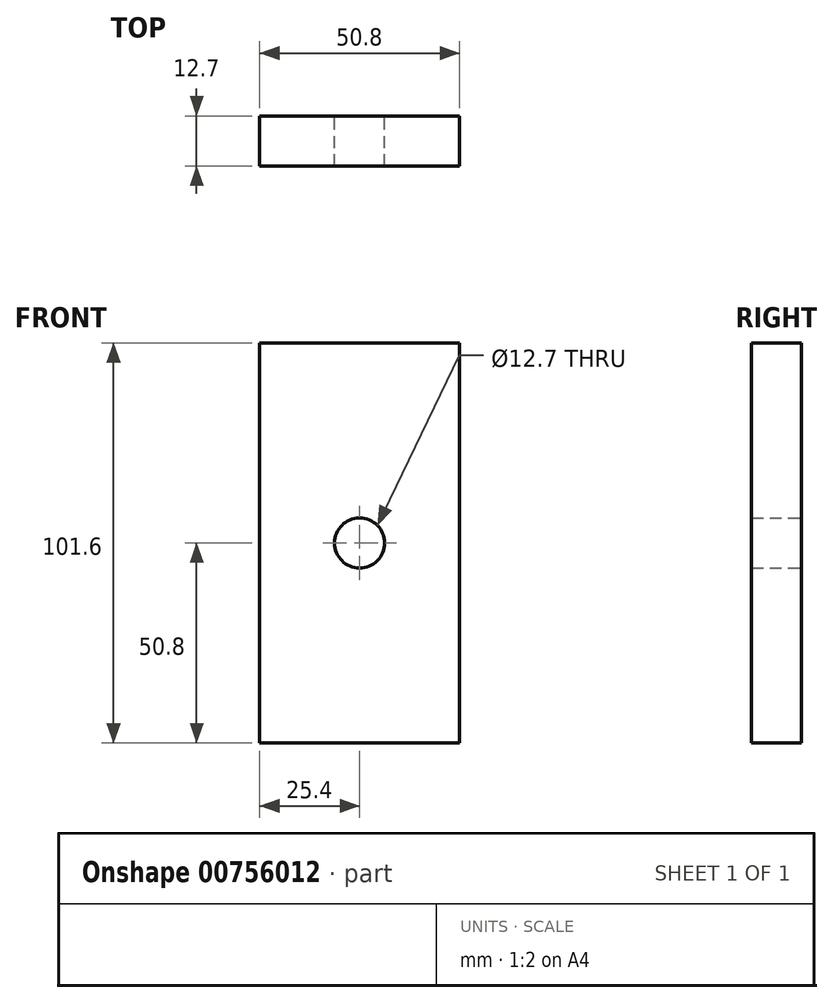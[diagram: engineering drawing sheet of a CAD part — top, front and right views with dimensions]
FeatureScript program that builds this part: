
annotation { "Feature Type Name" : "Feature", "Feature Type Description" : "" }
export const myFeature = defineFeature(function(context is Context, id is Id, definition is map)
    precondition{}
    {
        {
            var Q0;
            Q0=qCreatedBy(makeId("Front.planeOp"),FACE);
            var sketch = newSketch(context, id + "F0", { "sketchPlane" : qUnion([Q0])});
            skLineSegment(sketch, "E0.bottom", {"start": v(-25.4, 50.8) * mm, "end": v(25.4, 50.8) * mm});
            skLineSegment(sketch, "E0.top", {"start": v(-25.4, -50.8) * mm, "end": v(25.4, -50.8) * mm});
            skLineSegment(sketch, "E0.left", {"start": v(-25.4, 50.8) * mm, "end": v(-25.4, -50.8) * mm});
            skLineSegment(sketch, "E0.right", {"start": v(25.4, 50.8) * mm, "end": v(25.4, -50.8) * mm});
            skPoint(sketch, "E0.middle", {"position": v(0, 0) * mm});
            skCircle(sketch, "E1", {"center": v(0, 0) * mm, "radius": 6.35 * mm});
            skSolve(sketch);
        }
        {
            var Q0;
            Q0=makeQuery(id+"F0.imprint","IMPRINT",FACE,{"disambiguationData":[TD([[makeQuery(id+"F0.imprint","IMPRINT",EDGE,{"derivedFrom":sQuery(id+"F0.wireOp",EDGE,"E0.bottom")}),-1.0]])]});
            extrude(context, id + "F1", {"entities" : qUnion([Q0]), "depth" : 12.7 * mm, "offsetDistance" : 25.4 * mm});
        }
    });
